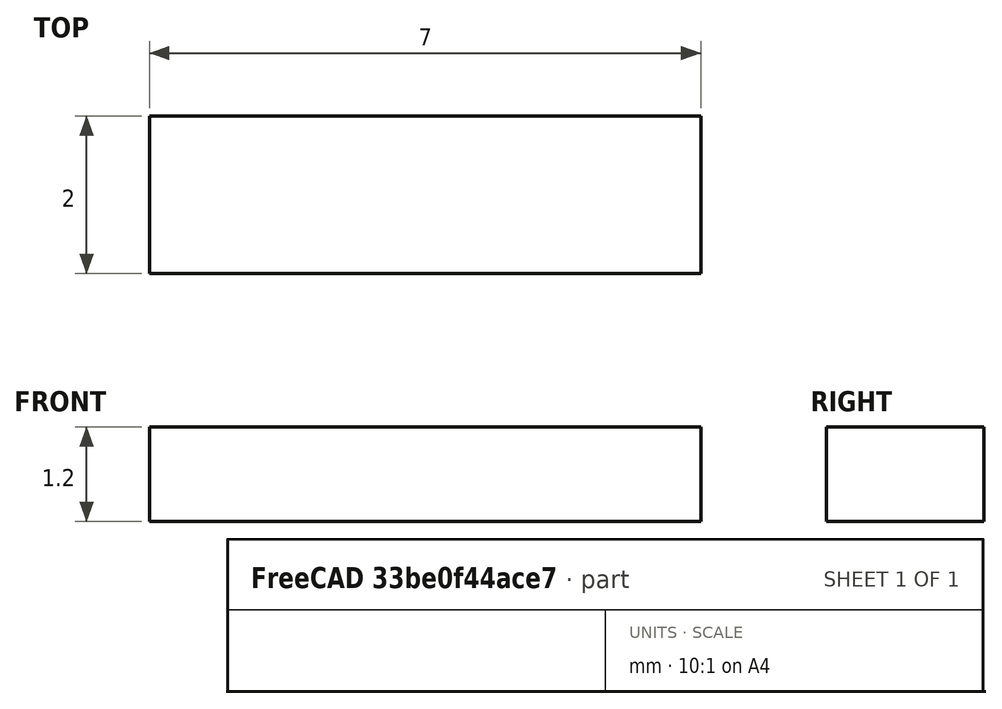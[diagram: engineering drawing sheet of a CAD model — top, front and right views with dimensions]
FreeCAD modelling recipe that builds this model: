
FCSTD DOCUMENT  (FreeCAD 0.16R6707 (Git))
Label: chip_ant_2x7
License: All rights reserved
LicenseURL: http://en.wikipedia.org/wiki/All_rights_reserved
objects: Sketcher::SketchObject×1, PartDesign::Pad×1
note: 3 computed .brp shape members not serialized (recipe doc carries the construction recipe); baked Part::Feature solids carry a one-line shape summary decoded from their .brp

FEATURE [Sketcher::SketchObject] Sketch
  sketch-geometry (5):
    g0: LineSegment StartX=-3.5 StartY=1 StartZ=0 EndX=3.5 EndY=1 EndZ=0
    g1: LineSegment StartX=3.5 StartY=1 StartZ=0 EndX=3.5 EndY=-1 EndZ=0
    g2: LineSegment StartX=3.5 StartY=-1 StartZ=0 EndX=-3.5 EndY=-1 EndZ=0
    g3: LineSegment StartX=-3.5 StartY=-1 StartZ=0 EndX=-3.5 EndY=1 EndZ=0
    g4: LineSegment [constr] StartX=0 StartY=0 StartZ=0 EndX=0 EndY=2.06425 EndZ=0
  constraints (14):
    c: Coincident(g0,g1)
    c: Coincident(g1,g2)
    c: Coincident(g2,g3)
    c: Coincident(g3,g0)
    c: Horizontal(g0)
    c: Horizontal(g2)
    c: Vertical(g1)
    c: Vertical(g3)
    c: DistanceX(g0,g0) = 7
    c: DistanceY(g3,g3) = 2
    c: Coincident(g4,g-1)
    c: Vertical(g4)
    c: Symmetric(g0,g0,g4)
    c: Symmetric(g1,g0,g-1)
FEATURE [PartDesign::Pad] Pad
  Length = 1.2
  Length2 = 100
  Sketch = -> Sketch
  Type = 0
